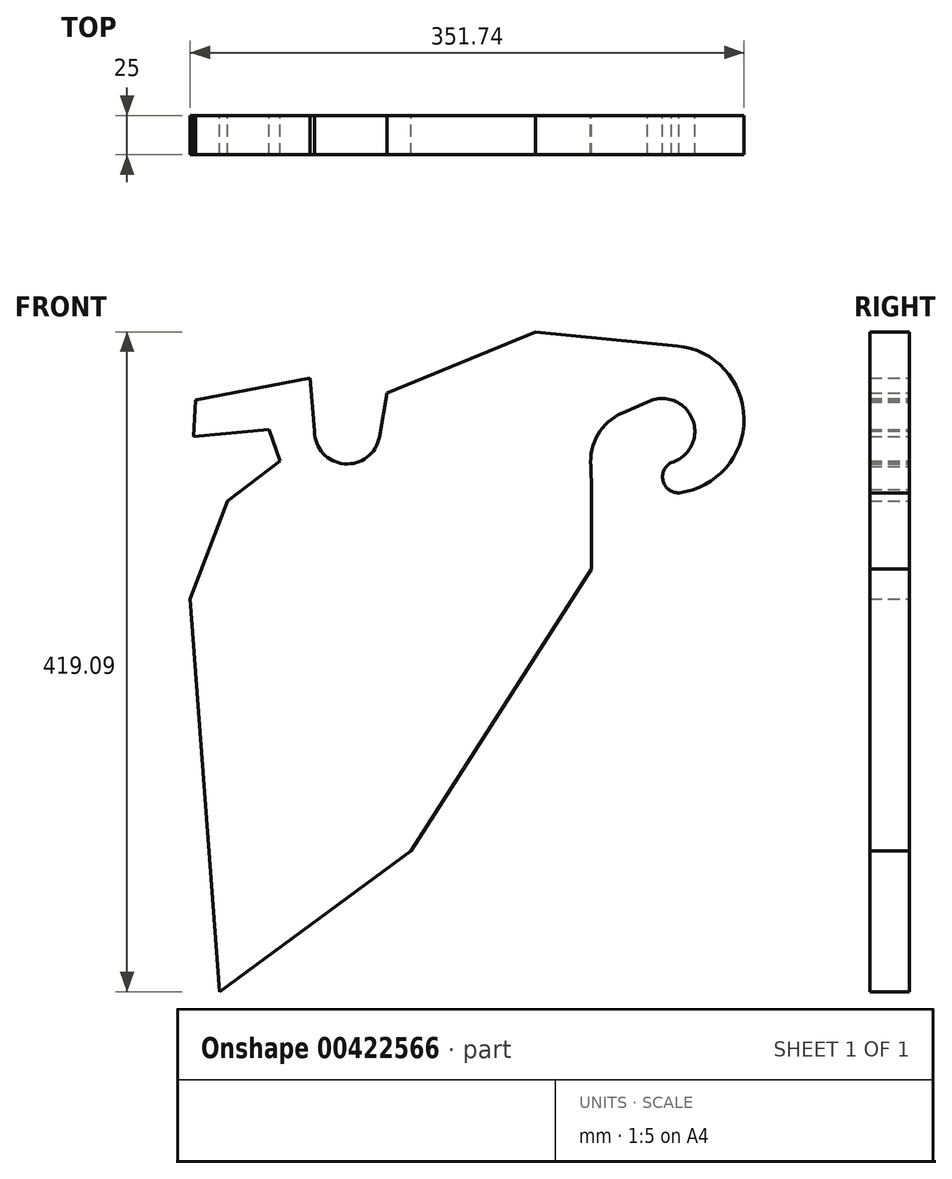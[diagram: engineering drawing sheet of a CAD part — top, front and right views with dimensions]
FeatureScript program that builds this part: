
annotation { "Feature Type Name" : "Feature", "Feature Type Description" : "" }
export const myFeature = defineFeature(function(context is Context, id is Id, definition is map)
    precondition{}
    {
        {
            var Q0;
            Q0=qCreatedBy(makeId("Front.planeOp"),FACE);
            var sketch = newSketch(context, id + "F0", { "sketchPlane" : qUnion([Q0])});
            skArc(sketch, "E0", {"start": v(-20.75, 0) * mm, "mid": v(-1.8, -20.67) * mm, "end": v(20.44, -3.57) * mm});
            skArc(sketch, "E1", {"start": v(202, -20.65) * mm, "mid": v(219.96, 5.67) * mm, "end": v(190.84, 18.62) * mm});
            skLineSegment(sketch, "E2", {"start": v(-223.61, 0) * mm, "end": v(377.72, 0) * mm});
            skLineSegment(sketch, "E3", {"start": v(-20.75, 0) * mm, "end": v(-23.71, 33.87) * mm});
            skLineSegment(sketch, "E4", {"start": v(25.31, 24.3) * mm, "end": v(119.63, 63.12) * mm});
            skArc(sketch, "E5", {"start": v(202, -39.4) * mm, "mid": v(251.85, 3.7) * mm, "end": v(209.6, 54.27) * mm});
            skLineSegment(sketch, "E6", {"start": v(119.63, 63.12) * mm, "end": v(209.6, 54.27) * mm});
            skLineSegment(sketch, "E7", {"start": v(200, 0) * mm, "end": v(202, 0) * mm});
            skLineSegment(sketch, "E8", {"start": v(202, -20.65) * mm, "end": v(202, -39.4) * mm});
            skLineSegment(sketch, "E9", {"start": v(-23.71, 33.87) * mm, "end": v(-96.35, 19.75) * mm});
            skLineSegment(sketch, "E10", {"start": v(-96.35, 19.75) * mm, "end": v(-97.56, -3.22) * mm});
            skLineSegment(sketch, "E11", {"start": v(-97.56, -3.22) * mm, "end": v(-49.74, 0.97) * mm});
            skLineSegment(sketch, "E12", {"start": v(-49.74, 0.97) * mm, "end": v(-42.56, -18.77) * mm});
            skLineSegment(sketch, "E13", {"start": v(-42.56, -18.77) * mm, "end": v(-75.88, -44.34) * mm});
            skLineSegment(sketch, "E14", {"start": v(200, 0) * mm, "end": v(154, 0) * mm});
            skLineSegment(sketch, "E15", {"start": v(154.63, -18) * mm, "end": v(155.29, -36.92) * mm});
            skArc(sketch, "E16", {"start": v(174.72, 11.63) * mm, "mid": v(159.21, -2.1) * mm, "end": v(154.78, -22.33) * mm});
            skLineSegment(sketch, "E17", {"start": v(192.68, 19.41) * mm, "end": v(174.72, 11.63) * mm});
            skLineSegment(sketch, "E18", {"start": v(-75.88, -44.34) * mm, "end": v(-99.74, -106.68) * mm});
            skLineSegment(sketch, "E19", {"start": v(-99.74, -106.68) * mm, "end": v(155.29, -87.45) * mm});
            skLineSegment(sketch, "E20", {"start": v(155.29, -87.45) * mm, "end": v(155.29, -36.92) * mm});
            skLineSegment(sketch, "E21", {"start": v(25.31, 24.3) * mm, "end": v(20.44, -3.57) * mm});
            skArc(sketch, "E22", {"start": v(205.91, -19.9) * mm, "mid": v(200.6, -31.48) * mm, "end": v(210.8, -39.14) * mm});
            skLineSegment(sketch, "E23", {"start": v(-99.74, -106.68) * mm, "end": v(-80.94, -355.97) * mm});
            skLineSegment(sketch, "E24", {"start": v(27.78, -97.06) * mm, "end": v(40.56, -266.58) * mm});
            skLineSegment(sketch, "E25", {"start": v(40.56, -266.58) * mm, "end": v(-80.94, -355.97) * mm});
            skLineSegment(sketch, "E26", {"start": v(40.56, -266.58) * mm, "end": v(155.29, -87.45) * mm});
            skSolve(sketch);
        }
        {
            var Q0;
            {var subQ0=sQuery(id+"F0.wireOp",EDGE,"E22");var subQ8=sQuery(id+"F0.wireOp",EDGE,"E1");var subQ10=makeQuery(id+"F0.imprint","INTERSECT",VERTEX,{"derivedFrom":[subQ8,subQ0]});Q0=makeQuery(id+"F0.imprint","IMPRINT",FACE,{"disambiguationData":[TD([[makeQuery(id+"F0.imprint","IMPRINT",EDGE,{"disambiguationData":[TD([[subQ10,-1.0]])],"derivedFrom":subQ8}),-1.0]])]});}
            var Q1;
            {var subQ0=sQuery(id+"F0.wireOp",EDGE,"E22");var subQ1=sQuery(id+"F0.wireOp",EDGE,"E8");var subQ2=makeQuery(id+"F0.imprint","INTERSECT",VERTEX,{"disambiguationData":[OD(0.0)],"derivedFrom":[subQ1,subQ0]});Q1=makeQuery(id+"F0.imprint","IMPRINT",FACE,{"disambiguationData":[TD([[makeQuery(id+"F0.imprint","IMPRINT",EDGE,{"disambiguationData":[TD([[subQ2,-1.0]])],"derivedFrom":subQ1}),-1.0]])]});}
            var Q2;
            {var subQ12=sQuery(id+"F0.wireOp",EDGE,"E4");Q2=makeQuery(id+"F0.imprint","IMPRINT",FACE,{"disambiguationData":[TD([[makeQuery(id+"F0.imprint","IMPRINT",EDGE,{"derivedFrom":subQ12}),-1.0]])]});}
            var Q3;
            {var subQ7=sQuery(id+"F0.wireOp",EDGE,"E0");Q3=makeQuery(id+"F0.imprint","IMPRINT",FACE,{"disambiguationData":[TD([[makeQuery(id+"F0.imprint","IMPRINT",EDGE,{"derivedFrom":subQ7}),-1.0]])]});}
            var Q4;
            {var subQ1=sQuery(id+"F0.wireOp",EDGE,"E3");Q4=makeQuery(id+"F0.imprint","IMPRINT",FACE,{"disambiguationData":[TD([[makeQuery(id+"F0.imprint","IMPRINT",EDGE,{"derivedFrom":subQ1}),1.0]])]});}
            var Q5;
            {var subQ0=sQuery(id+"F0.wireOp",EDGE,"E10");var subQ1=sQuery(id+"F0.wireOp",EDGE,"E2");var subQ2=makeQuery(id+"F0.imprint","INTERSECT",VERTEX,{"derivedFrom":[subQ1,subQ0]});Q5=makeQuery(id+"F0.imprint","IMPRINT",FACE,{"disambiguationData":[TD([[makeQuery(id+"F0.imprint","IMPRINT",EDGE,{"disambiguationData":[TD([[subQ2,-1.0]])],"derivedFrom":subQ1}),-1.0]])]});}
            var Q6;
            {var subQ0=sQuery(id+"F0.wireOp",EDGE,"E23");Q6=makeQuery(id+"F0.imprint","IMPRINT",FACE,{"disambiguationData":[TD([[makeQuery(id+"F0.imprint","IMPRINT",EDGE,{"derivedFrom":subQ0}),1.0]])]});}
            var Q7;
            {var subQ2=sQuery(id+"F0.wireOp",EDGE,"E24");Q7=makeQuery(id+"F0.imprint","IMPRINT",FACE,{"disambiguationData":[TD([[makeQuery(id+"F0.imprint","IMPRINT",EDGE,{"derivedFrom":subQ2}),1.0]])]});}
            extrude(context, id + "F1", {"entities" : qUnion([Q0, Q1, Q2, Q3, Q4, Q5, Q6, Q7]), "depth" : 25 * mm, "offsetDistance" : 25 * mm});
        }
    });
